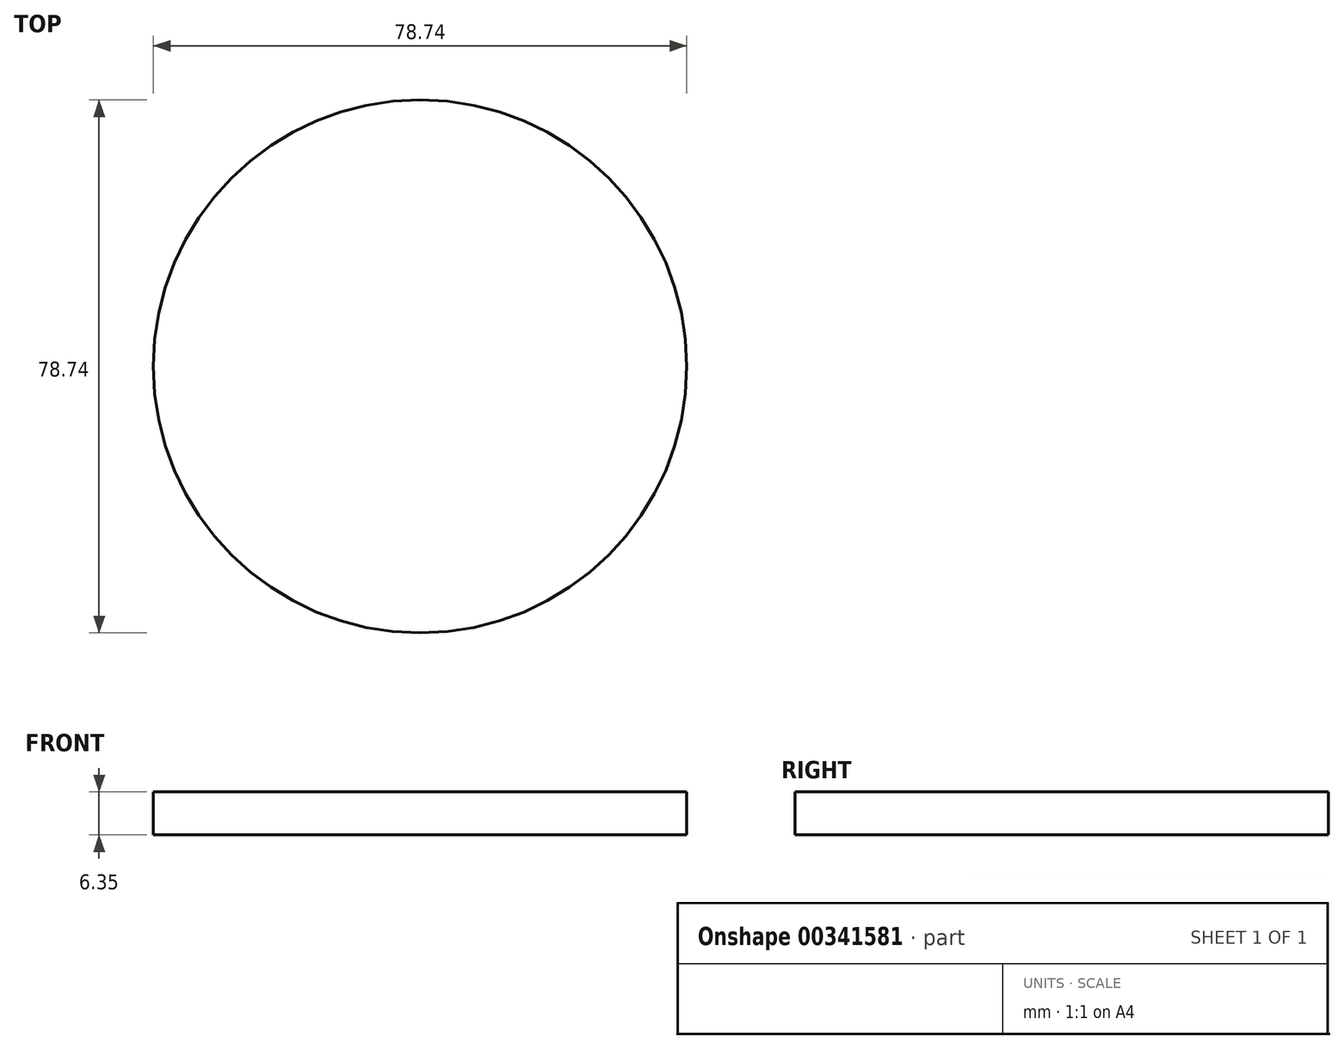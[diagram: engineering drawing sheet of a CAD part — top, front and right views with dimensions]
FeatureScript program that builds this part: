
annotation { "Feature Type Name" : "Feature", "Feature Type Description" : "" }
export const myFeature = defineFeature(function(context is Context, id is Id, definition is map)
    precondition{}
    {
        {
            var Q0;
            Q0=qCreatedBy(makeId("Top.planeOp"),FACE);
            var sketch = newSketch(context, id + "F0", { "sketchPlane" : qUnion([Q0])});
            skCircle(sketch, "E0", {"center": v(0, 0) * mm, "radius": 33.02 * mm});
            skCircle(sketch, "E1", {"center": v(0, 0) * mm, "radius": 39.37 * mm});
            skArc(sketch, "E2", {"start": v(-1.97, -32.96) * mm, "mid": v(-1.43, -31.27) * mm, "end": v(-0.7, -29.64) * mm});
            skArc(sketch, "E3", {"start": v(1.97, -32.96) * mm, "mid": v(1.42, -31.27) * mm, "end": v(0.68, -29.65) * mm});
            skArc(sketch, "E4", {"start": v(-0.7, -29.64) * mm, "mid": v(0, -29.63) * mm, "end": v(0.68, -29.65) * mm});
            skSolve(sketch);
        }
        {
            var Q0;
            Q0 = qSketchRegion(id + "F0", true);
            var Q1;
            {var subQ0=sQuery(id+"F0.wireOp",EDGE,"E2");Q1=makeQuery(id+"F0.imprint","IMPRINT",FACE,{"disambiguationData":[TD([[makeQuery(id+"F0.imprint","IMPRINT",EDGE,{"derivedFrom":subQ0}),-1.0]])]});}
            extrude(context, id + "F1", {"entities" : qUnion([Q0, Q1]), "depth" : 6.35 * mm});
        }
        {
            var Q0;
            Q0=makeQuery(id+"F1.opExtrude","SWEPT_BODY",BODY,{"disambiguationData":[OSD([sQuery(id+"F0.wireOp",EDGE,"E0"),sQuery(id+"F0.wireOp",EDGE,"E1"),sQuery(id+"F0.wireOp",EDGE,"E2"),sQuery(id+"F0.wireOp",EDGE,"E3"),sQuery(id+"F0.wireOp",EDGE,"E4")])]});
            var Q1;
            Q1=makeQuery(id+"F1.opExtrude","SWEPT_FACE",FACE,{"disambiguationData":[OSD([sQuery(id+"F0.wireOp",EDGE,"E0")])]});
            circularPattern(context, id + "F2", {"operationType" : NewBodyOperationType.ADD, "entities" : qUnion([Q0]), "axis" : qUnion([Q1]), "angle" : 360 * degree, "instanceCount" : 30, "equalSpace" : true});
        }
    });
